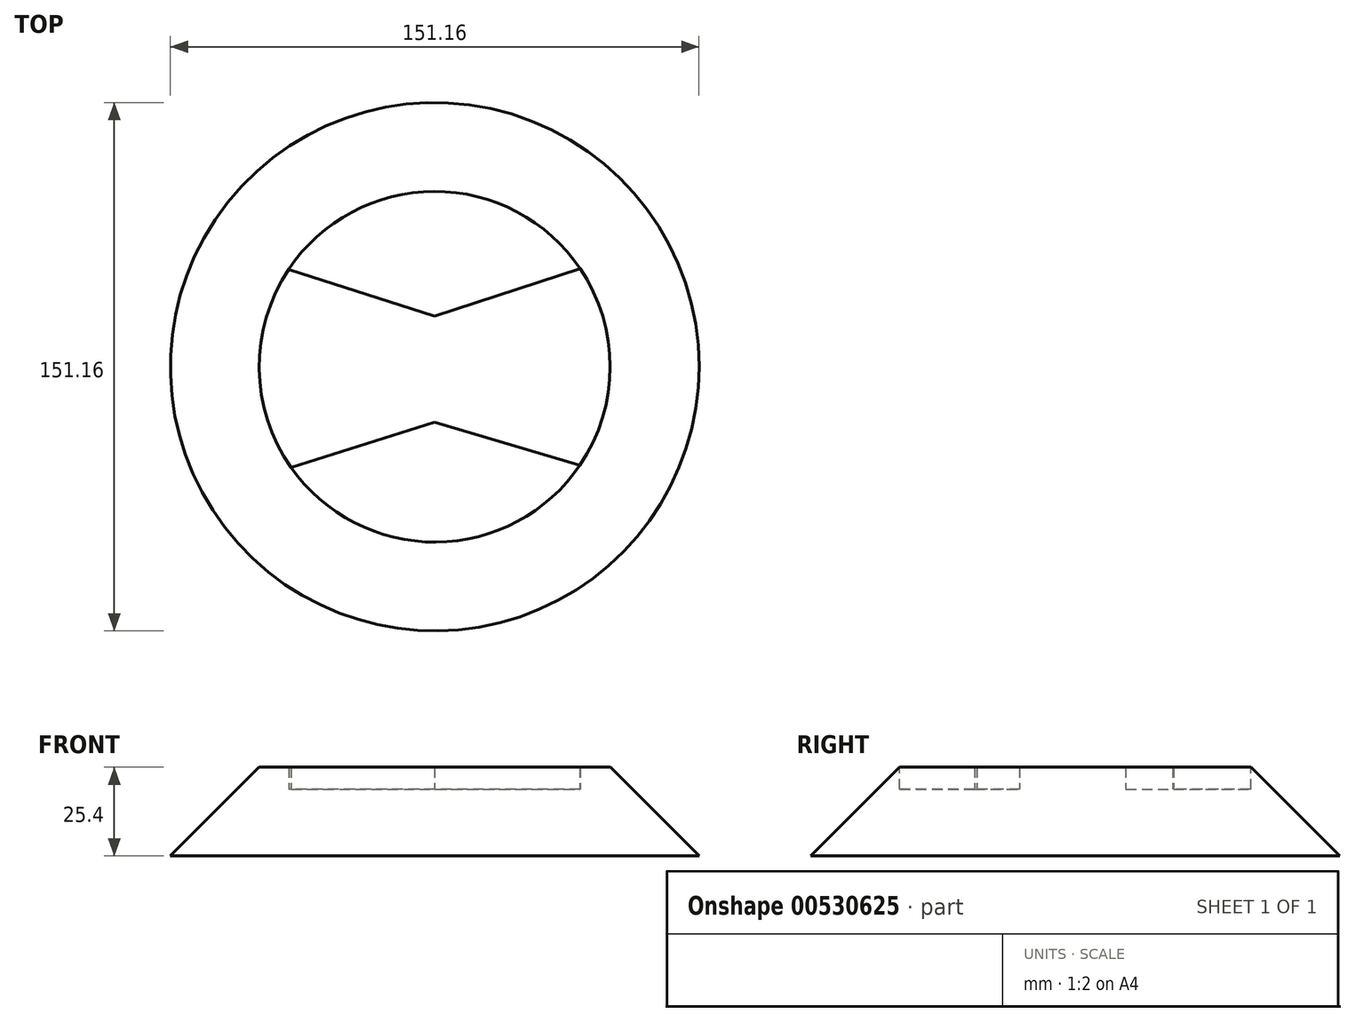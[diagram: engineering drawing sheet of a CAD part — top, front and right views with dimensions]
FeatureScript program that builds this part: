
annotation { "Feature Type Name" : "Feature", "Feature Type Description" : "" }
export const myFeature = defineFeature(function(context is Context, id is Id, definition is map)
    precondition{}
    {
        {
            var Q0;
            Q0=qCreatedBy(makeId("Top.planeOp"),FACE);
            var sketch = newSketch(context, id + "F0", { "sketchPlane" : qUnion([Q0])});
            skCircle(sketch, "E0", {"center": v(0, 0) * mm, "radius": 75.58 * mm});
            skSolve(sketch);
        }
        {
            var Q0;
            Q0=makeQuery(id+"F0.imprint","IMPRINT",FACE,{"disambiguationData":[TD([[makeQuery(id+"F0.imprint","IMPRINT",EDGE,{"derivedFrom":sQuery(id+"F0.wireOp",EDGE,"E0")}),1.0]])]});
            extrude(context, id + "F1", {"entities" : qUnion([Q0]), "depth" : 25.4 * mm, "offsetDistance" : 25.4 * mm});
        }
        {
            var Q0;
            Q0=makeQuery(id+"F1.opExtrude","CAP_EDGE",EDGE,{"disambiguationData":[OSD([sQuery(id+"F0.wireOp",EDGE,"E0")])],"isStart":false});
            chamfer(context, id + "F2", {"entities" : qUnion([Q0]), "width" : 25.4 * mm, "tangentPropagation" : true});
        }
        {
            var Q0;
            Q0=makeQuery(id+"F1.opExtrude","CAP_FACE",FACE,{"disambiguationData":[OSD([sQuery(id+"F0.wireOp",EDGE,"E0")])],"isStart":false});
            extrude(context, id + "F3", {"entities" : qUnion([Q0]), "operationType" : NewBodyOperationType.REMOVE, "oppositeDirection" : true, "depth" : 12.7 * mm, "offsetDistance" : 25.4 * mm});
        }
        {
            var Q0;
            Q0=makeQuery(id+"F3.boolean.opBoolean","COPY",FACE,{"derivedFrom":makeQuery(id+"F3.opExtrude","CAP_FACE",FACE,{"disambiguationData":[OSD([sQuery(id+"F0.wireOp",EDGE,"E0")])],"isStart":false})});
            var sketch = newSketch(context, id + "F4", { "sketchPlane" : qUnion([Q0])});
            skLineSegment(sketch, "E1", {"start": v(-41.07, -28.83) * mm, "end": v(0, -15.93) * mm});
            skLineSegment(sketch, "E2", {"start": v(0, -15.93) * mm, "end": v(0, 14.45) * mm});
            skLineSegment(sketch, "E3", {"start": v(0, 14.45) * mm, "end": v(-41.73, 27.88) * mm});
            skLineSegment(sketch, "E4", {"start": v(0, -15.93) * mm, "end": v(41.53, -28.17) * mm});
            skLineSegment(sketch, "E5", {"start": v(0, 14.45) * mm, "end": v(41.59, 28.08) * mm});
            skSolve(sketch);
        }
        {
            var Q0;
            Q0=makeQuery(id+"F4.imprint","IMPRINT",FACE,{"disambiguationData":[TD([[makeQuery(id+"F4.imprint","IMPRINT",EDGE,{"derivedFrom":sQuery(id+"F4.wireOp",EDGE,"E2")}),-1.0]])]});
            var Q1;
            {var subQ0=sQuery(id+"F4.wireOp",EDGE,"E1");Q1=makeQuery(id+"F4.imprint","IMPRINT",FACE,{"disambiguationData":[TD([[makeQuery(id+"F4.imprint","IMPRINT",EDGE,{"derivedFrom":subQ0}),1.0]])]});}
            extrude(context, id + "F5", {"entities" : qUnion([Q0, Q1]), "operationType" : NewBodyOperationType.ADD, "depth" : 12.7 * mm, "offsetDistance" : 25.4 * mm});
        }
        {
            var Q0;
            {var subQ0=sQuery(id+"F0.wireOp",EDGE,"E0");Q0=makeQuery(id+"F5.boolean.opBoolean","SPLIT",FACE,{"disambiguationData":[TD([makeQuery(id+"F5.opExtrude","SWEPT_FACE",FACE,{"disambiguationData":[OSD([sQuery(id+"F4.wireOp",EDGE,"E1")])]})])],"derivedFrom":makeQuery(id+"F3.boolean.opBoolean","COPY",FACE,{"derivedFrom":makeQuery(id+"F3.opExtrude","CAP_FACE",FACE,{"disambiguationData":[OSD([subQ0])],"isStart":false})})});}
            extrude(context, id + "F6", {"entities" : qUnion([Q0]), "operationType" : NewBodyOperationType.ADD, "depth" : 6.35 * mm, "offsetDistance" : 25.4 * mm});
        }
        {
            var Q0;
            {var subQ0=sQuery(id+"F0.wireOp",EDGE,"E0");Q0=makeQuery(id+"F5.boolean.opBoolean","SPLIT",FACE,{"disambiguationData":[TD([makeQuery(id+"F5.opExtrude","SWEPT_FACE",FACE,{"disambiguationData":[OSD([sQuery(id+"F4.wireOp",EDGE,"E3")])]})])],"derivedFrom":makeQuery(id+"F3.boolean.opBoolean","COPY",FACE,{"derivedFrom":makeQuery(id+"F3.opExtrude","CAP_FACE",FACE,{"disambiguationData":[OSD([subQ0])],"isStart":false})})});}
            extrude(context, id + "F7", {"entities" : qUnion([Q0]), "operationType" : NewBodyOperationType.ADD, "depth" : 6.35 * mm, "offsetDistance" : 25.4 * mm});
        }
    });
